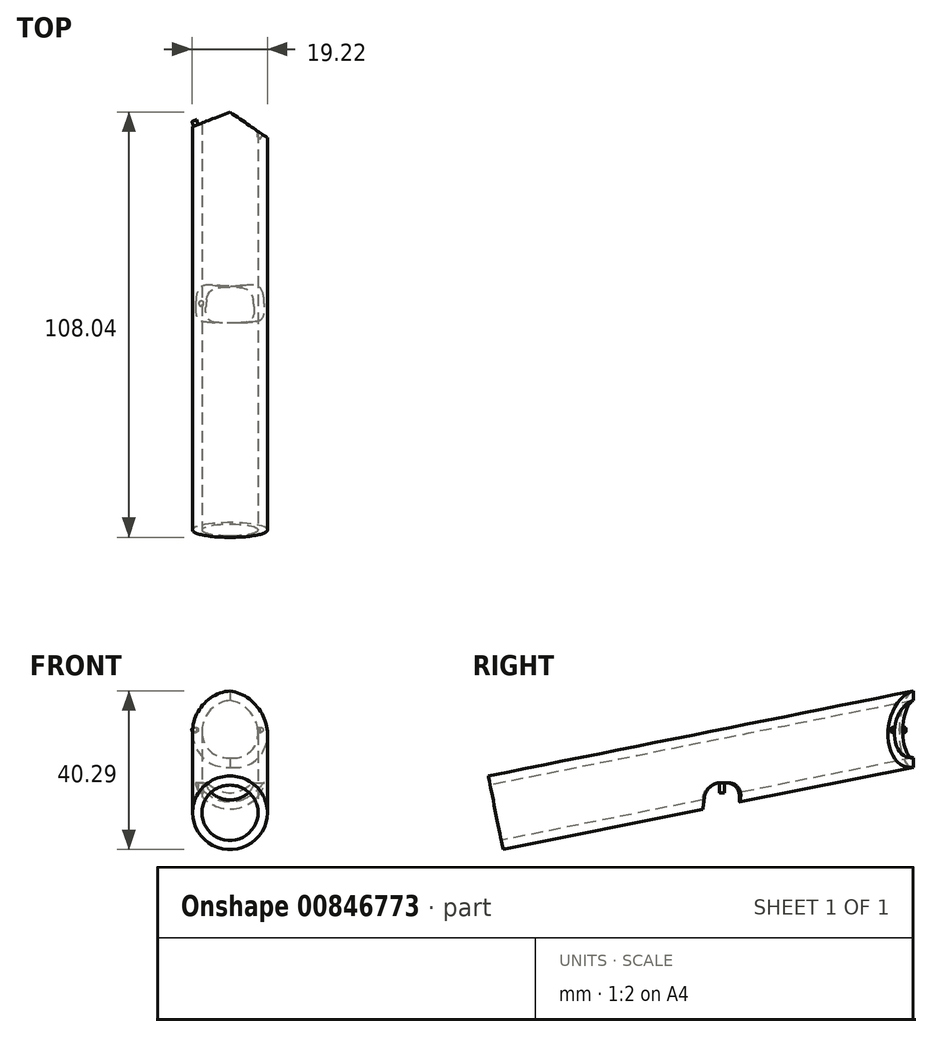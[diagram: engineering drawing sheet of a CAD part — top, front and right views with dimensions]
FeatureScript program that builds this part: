
annotation { "Feature Type Name" : "Feature", "Feature Type Description" : "" }
export const myFeature = defineFeature(function(context is Context, id is Id, definition is map)
    precondition{}
    {
        {
            var Q0;
            Q0=qCreatedBy(makeId("Front.planeOp"),FACE);
            var sketch = newSketch(context, id + "F0", { "sketchPlane" : qUnion([Q0])});
            skLineSegment(sketch, "E0", {"start": v(-25.47, 0) * mm, "end": v(29.78, 0) * mm});
            skSolve(sketch);
        }
        {
            var Q0;
            Q0=sQuery(id+"F0.wireOp",EDGE,"E0");
            cPlane(context, id + "F1", {"entities" : qUnion([Q0]), "cplaneType" : CPlaneType.LINE_ANGLE, "offset" : 25.4 * mm, "angle" : 11.3 * degree, "width" : 152.4 * mm, "height" : 152.4 * mm});
        }
        {
            var Q0;
            Q0=qCreatedBy(id+"F1.planeOp",FACE);
            var sketch = newSketch(context, id + "F2", { "sketchPlane" : qUnion([Q0])});
            skCircle(sketch, "E1", {"center": v(0, 0) * mm, "radius": 7.14 * mm});
            skCircle(sketch, "E2", {"center": v(0, 0) * mm, "radius": 9.53 * mm});
            skSolve(sketch);
        }
        {
            var Q0;
            Q0=makeQuery(id+"F2.imprint","IMPRINT",FACE,{"disambiguationData":[TD([[makeQuery(id+"F2.imprint","IMPRINT",EDGE,{"derivedFrom":sQuery(id+"F2.wireOp",EDGE,"E1")}),-1.0]])]});
            extrude(context, id + "F3", {"entities" : qUnion([Q0]), "depth" : 114.3 * mm, "offsetDistance" : 25.4 * mm});
        }
        {
            var Q0;
            Q0=qCreatedBy(makeId("Top.planeOp"),FACE);
            var sketch = newSketch(context, id + "F4", { "sketchPlane" : qUnion([Q0])});
            skLineSegment(sketch, "E3", {"start": v(0, 0) * mm, "end": v(0, 139.91) * mm, "construction": true});
            skLineSegment(sketch, "E4", {"start": v(-27.69, 99.06) * mm, "end": v(29.95, 99.06) * mm, "construction": true});
            skLineSegment(sketch, "E5", {"start": v(10.39, 99.06) * mm, "end": v(0, 106.17) * mm});
            skLineSegment(sketch, "E6", {"start": v(-9.53, 105.28) * mm, "end": v(-9.53, 134.07) * mm});
            skLineSegment(sketch, "E7", {"start": v(-9.53, 134.07) * mm, "end": v(10.39, 134.07) * mm});
            skLineSegment(sketch, "E8", {"start": v(10.39, 134.07) * mm, "end": v(10.39, 99.06) * mm});
            skLineSegment(sketch, "E9", {"start": v(0, 106.17) * mm, "end": v(-9.52, 102.48) * mm});
            skLineSegment(sketch, "E10", {"start": v(-9.52, 105.28) * mm, "end": v(-9.52, 102.48) * mm});
            skSolve(sketch);
        }
        {
            var Q0;
            Q0=qSketchRegion(id+"F4",true);
            extrude(context, id + "F5", {"entities" : qUnion([Q0]), "operationType" : NewBodyOperationType.REMOVE, "depth" : 127 * mm, "offsetDistance" : 25.4 * mm});
        }
        {
            var Q0;
            Q0=qCreatedBy(makeId("Top.planeOp"),FACE);
            var sketch = newSketch(context, id + "F6", { "sketchPlane" : qUnion([Q0])});
            skCircle(sketch, "E11", {"center": v(0, 106.17) * mm, "radius": 53.6 * mm});
            skCircle(sketch, "E12", {"center": v(0, 106.17) * mm, "radius": 44.2 * mm});
            skSolve(sketch);
        }
        {
            var Q0;
            Q0=makeQuery(id+"F6.imprint","IMPRINT",FACE,{"disambiguationData":[TD([[makeQuery(id+"F6.imprint","IMPRINT",EDGE,{"derivedFrom":sQuery(id+"F6.wireOp",EDGE,"E11")}),1.0]])]});
            extrude(context, id + "F7", {"entities" : qUnion([Q0]), "operationType" : NewBodyOperationType.REMOVE, "depth" : 7.62 * mm, "offsetDistance" : 25.4 * mm});
        }
        {
            var Q0;
            Q0=makeQuery(id+"F7.boolean.opBoolean","COPY",EDGE,{"disambiguationData":[OD(0.0)],"derivedFrom":makeQuery(id+"F7.opExtrude","CAP_EDGE",EDGE,{"disambiguationData":[OSD([sQuery(id+"F6.wireOp",EDGE,"E12")])],"isStart":false})});
            var Q1;
            Q1=makeQuery(id+"F7.boolean.opBoolean","COPY",EDGE,{"disambiguationData":[OD(1.0)],"derivedFrom":makeQuery(id+"F7.opExtrude","CAP_EDGE",EDGE,{"disambiguationData":[OSD([sQuery(id+"F6.wireOp",EDGE,"E11")])],"isStart":false})});
            var Q2;
            Q2=makeQuery(id+"F7.boolean.opBoolean","COPY",EDGE,{"disambiguationData":[OD(1.0)],"derivedFrom":makeQuery(id+"F7.opExtrude","CAP_EDGE",EDGE,{"disambiguationData":[OSD([sQuery(id+"F6.wireOp",EDGE,"E12")])],"isStart":false})});
            var Q3;
            Q3=makeQuery(id+"F7.boolean.opBoolean","COPY",EDGE,{"disambiguationData":[OD(0.0)],"derivedFrom":makeQuery(id+"F7.opExtrude","CAP_EDGE",EDGE,{"disambiguationData":[OSD([sQuery(id+"F6.wireOp",EDGE,"E11")])],"isStart":false})});
            fillet(context, id + "F8", {"entities" : qUnion([Q0, Q1, Q2, Q3]), "radius" : 3.8 * mm, "tangentPropagation" : true, "allowEdgeOverflow" : false});
        }
        {
            var Q0;
            Q0=makeQuery(id+"F5.boolean.opBoolean","COPY",FACE,{"derivedFrom":makeQuery(id+"F5.opExtrude","SWEPT_FACE",FACE,{"disambiguationData":[OSD([sQuery(id+"F4.wireOp",EDGE,"E5")])]})});
            var sketch = newSketch(context, id + "F9", { "sketchPlane" : qUnion([Q0])});
            skCircle(sketch, "E13", {"center": v(50.46, 21.05) * mm, "radius": 0.64 * mm});
            skSolve(sketch);
        }
        {
            var Q0;
            Q0=makeQuery(id+"F9.imprint","IMPRINT",FACE,{"disambiguationData":[TD([[makeQuery(id+"F9.imprint","IMPRINT",EDGE,{"derivedFrom":sQuery(id+"F9.wireOp",EDGE,"E13")}),1.0]])]});
            var Q1;
            Q1=sQuery(id+"F9.wireOp",EDGE,"E13");
            extrude(context, id + "F10", {"entities" : qUnion([Q0]), "operationType" : NewBodyOperationType.REMOVE, "surfaceEntities" : qUnion([Q1]), "oppositeDirection" : true, "depth" : 1.27 * mm, "offsetDistance" : 25.4 * mm});
        }
        {
            var Q0;
            Q0=qCreatedBy(makeId("Top.planeOp"),FACE);
            var sketch = newSketch(context, id + "F11", { "sketchPlane" : qUnion([Q0])});
            skCircle(sketch, "E14", {"center": v(0, 111.53) * mm, "radius": 38.1 * mm, "construction": true});
            skLineSegment(sketch, "E15", {"start": v(0, 29.2) * mm, "end": v(0, 94.83) * mm, "construction": true});
            skCircle(sketch, "E16", {"center": v(0, 85.5) * mm, "radius": 0.64 * mm});
            skSolve(sketch);
        }
        {
            var Q0;
            Q0=makeQuery(id+"F5.boolean.opBoolean","COPY",FACE,{"derivedFrom":makeQuery(id+"F5.opExtrude","SWEPT_FACE",FACE,{"disambiguationData":[OSD([sQuery(id+"F4.wireOp",EDGE,"E9")])]})});
            var sketch = newSketch(context, id + "F12", { "sketchPlane" : qUnion([Q0])});
            skCircle(sketch, "E17", {"center": v(-29.12, 21.05) * mm, "radius": 0.64 * mm});
            skSolve(sketch);
        }
        {
            var Q0;
            Q0=makeQuery(id+"F12.imprint","IMPRINT",FACE,{"disambiguationData":[TD([[makeQuery(id+"F12.imprint","IMPRINT",EDGE,{"derivedFrom":sQuery(id+"F12.wireOp",EDGE,"E17")}),1.0]])]});
            extrude(context, id + "F13", {"entities" : qUnion([Q0]), "operationType" : NewBodyOperationType.ADD, "depth" : 1.27 * mm, "offsetDistance" : 25.4 * mm});
        }
        {
            var Q0;
            Q0=qCreatedBy(makeId("Top.planeOp"),FACE);
            var sketch = newSketch(context, id + "F14", { "sketchPlane" : qUnion([Q0])});
            skLineSegment(sketch, "E18.bottom", {"start": v(0, 5.7) * mm, "end": v(-3.47, 5.7) * mm});
            skLineSegment(sketch, "E18.top", {"start": v(0, 8.76) * mm, "end": v(-3.47, 8.76) * mm});
            skLineSegment(sketch, "E18.left", {"start": v(0, 5.7) * mm, "end": v(0, 8.76) * mm});
            skLineSegment(sketch, "E18.right", {"start": v(-3.47, 5.7) * mm, "end": v(-3.47, 8.76) * mm});
            skSolve(sketch);
        }
        {
            var Q0;
            Q0=makeQuery(id+"F7.boolean.opBoolean","COPY",FACE,{"disambiguationData":[OD(0.0)],"derivedFrom":makeQuery(id+"F7.opExtrude","CAP_FACE",FACE,{"disambiguationData":[OSD([sQuery(id+"F6.wireOp",EDGE,"E11"),sQuery(id+"F6.wireOp",EDGE,"E12")])],"isStart":false})});
            var sketch = newSketch(context, id + "F15", { "sketchPlane" : qUnion([Q0])});
            skCircle(sketch, "E19", {"center": v(-7.3, -57.53) * mm, "radius": 0.64 * mm});
            skSolve(sketch);
        }
        {
            var Q0;
            {var subQ0=sQuery(id+"F15.wireOp",EDGE,"E19");var subQ1=sQuery(id+"F6.wireOp",EDGE,"E12");var subQ2=sQuery(id+"F6.wireOp",EDGE,"E11");var subQ3=makeQuery(id+"F7.boolean.opBoolean","COPY",FACE,{"disambiguationData":[OD(0.0)],"derivedFrom":makeQuery(id+"F7.opExtrude","CAP_FACE",FACE,{"disambiguationData":[OSD([subQ2,subQ1])],"isStart":false})});var subQ4=makeQuery(id+"F8.opFillet","BLEND_EDGE",EDGE,{"blendedFrom":[makeQuery(id+"F7.boolean.opBoolean","COPY",EDGE,{"disambiguationData":[OD(0.0)],"derivedFrom":makeQuery(id+"F7.opExtrude","CAP_EDGE",EDGE,{"disambiguationData":[OSD([subQ2])],"isStart":false})}),subQ3],"blendedInto":[subQ3]});var subQ5=makeQuery(id+"F15.imprint","INTERSECT",VERTEX,{"disambiguationData":[OD(0.0)],"derivedFrom":[subQ4,subQ0]});Q0=makeQuery(id+"F15.imprint","IMPRINT",FACE,{"disambiguationData":[TD([[makeQuery(id+"F15.imprint","IMPRINT",EDGE,{"disambiguationData":[TD([[subQ5,-1.0]])],"derivedFrom":subQ0}),1.0]])]});}
            var Q1;
            {var subQ0=sQuery(id+"F15.wireOp",EDGE,"E19");var subQ1=sQuery(id+"F6.wireOp",EDGE,"E11");var subQ2=makeQuery(id+"F8.opFillet","BLEND_EDGE",EDGE,{"blendedFrom":[makeQuery(id+"F7.boolean.opBoolean","COPY",EDGE,{"disambiguationData":[OD(0.0)],"derivedFrom":makeQuery(id+"F7.opExtrude","CAP_EDGE",EDGE,{"disambiguationData":[OSD([subQ1])],"isStart":false})}),makeQuery(id+"F7.boolean.opBoolean","COPY",FACE,{"disambiguationData":[OD(0.0)],"derivedFrom":makeQuery(id+"F7.opExtrude","CAP_FACE",FACE,{"disambiguationData":[OSD([subQ1,sQuery(id+"F6.wireOp",EDGE,"E12")])],"isStart":false})})],"blendedInto":[makeQuery(id+"F7.boolean.opBoolean","COPY",FACE,{"disambiguationData":[OD(0.0)],"derivedFrom":makeQuery(id+"F7.opExtrude","CAP_FACE",FACE,{"disambiguationData":[OSD([subQ1,sQuery(id+"F6.wireOp",EDGE,"E12")])],"isStart":false})})]});var subQ3=makeQuery(id+"F15.imprint","INTERSECT",VERTEX,{"disambiguationData":[OD(0.0)],"derivedFrom":[subQ2,subQ0]});Q1=makeQuery(id+"F15.imprint","IMPRINT",FACE,{"disambiguationData":[TD([[makeQuery(id+"F15.imprint","IMPRINT",EDGE,{"disambiguationData":[TD([[subQ3,1.0]])],"derivedFrom":subQ0}),1.0]])]});}
            var Q2;
            {var subQ0=sQuery(id+"F15.wireOp",EDGE,"E19");var subQ1=sQuery(id+"F6.wireOp",EDGE,"E12");var subQ2=makeQuery(id+"F8.opFillet","BLEND_EDGE",EDGE,{"blendedFrom":[makeQuery(id+"F7.boolean.opBoolean","COPY",EDGE,{"disambiguationData":[OD(0.0)],"derivedFrom":makeQuery(id+"F7.opExtrude","CAP_EDGE",EDGE,{"disambiguationData":[OSD([subQ1])],"isStart":false})}),makeQuery(id+"F7.boolean.opBoolean","COPY",FACE,{"disambiguationData":[OD(0.0)],"derivedFrom":makeQuery(id+"F7.opExtrude","CAP_FACE",FACE,{"disambiguationData":[OSD([sQuery(id+"F6.wireOp",EDGE,"E11"),subQ1])],"isStart":false})})],"blendedInto":[makeQuery(id+"F7.boolean.opBoolean","COPY",FACE,{"disambiguationData":[OD(0.0)],"derivedFrom":makeQuery(id+"F7.opExtrude","CAP_FACE",FACE,{"disambiguationData":[OSD([sQuery(id+"F6.wireOp",EDGE,"E11"),subQ1])],"isStart":false})})]});var subQ3=makeQuery(id+"F15.imprint","INTERSECT",VERTEX,{"disambiguationData":[OD(0.0)],"derivedFrom":[subQ2,subQ0]});Q2=makeQuery(id+"F15.imprint","IMPRINT",FACE,{"disambiguationData":[TD([[makeQuery(id+"F15.imprint","IMPRINT",EDGE,{"disambiguationData":[TD([[subQ3,-1.0]])],"derivedFrom":subQ0}),1.0]])]});}
            var Q3;
            Q3=sQuery(id+"F15.wireOp",EDGE,"E19");
            extrude(context, id + "F16", {"entities" : qUnion([Q0, Q1, Q2]), "operationType" : NewBodyOperationType.ADD, "surfaceEntities" : qUnion([Q3]), "depth" : 2.54 * mm, "offsetDistance" : 25.4 * mm});
        }
    });
